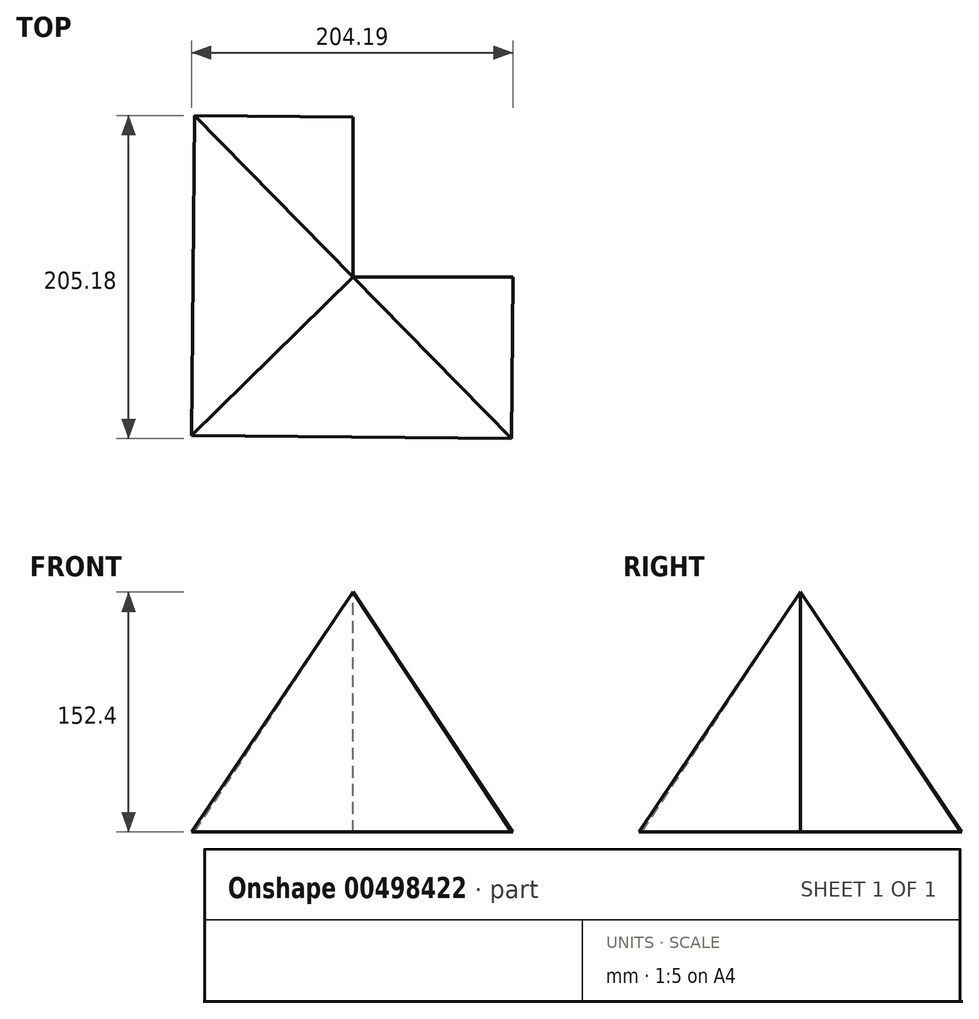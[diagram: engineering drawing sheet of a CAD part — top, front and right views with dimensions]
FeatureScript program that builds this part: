
annotation { "Feature Type Name" : "Feature", "Feature Type Description" : "" }
export const myFeature = defineFeature(function(context is Context, id is Id, definition is map)
    precondition{}
    {
        {
            var Q0;
            Q0=qCreatedBy(makeId("Top.planeOp"),FACE);
            var sketch = newSketch(context, id + "F0", { "sketchPlane" : qUnion([Q0])});
            skCircle(sketch, "E0.cCircle", {"center": v(0, 0) * mm, "radius": 143.68 * mm, "construction": true});
            skLineSegment(sketch, "E0.0", {"start": v(-100.6, 102.6) * mm, "end": v(102.6, 100.6) * mm});
            skLineSegment(sketch, "E0.1", {"start": v(102.6, 100.6) * mm, "end": v(100.6, -102.6) * mm});
            skLineSegment(sketch, "E0.2", {"start": v(100.6, -102.6) * mm, "end": v(-102.6, -100.6) * mm});
            skLineSegment(sketch, "E0.3", {"start": v(-102.6, -100.6) * mm, "end": v(-100.6, 102.6) * mm});
            skSolve(sketch);
        }
        {
            var Q0;
            Q0=qCreatedBy(makeId("Top.planeOp"),FACE);
            cPlane(context, id + "F1", {"entities" : qUnion([Q0]), "cplaneType" : CPlaneType.OFFSET, "offset" : 152.4 * mm, "width" : 152.4 * mm, "height" : 152.4 * mm});
        }
        {
            var Q0;
            Q0=qCreatedBy(id+"F1.planeOp",FACE);
            var sketch = newSketch(context, id + "F2", { "sketchPlane" : qUnion([Q0])});
            skPoint(sketch, "E1", {"position": v(0, 0) * mm});
            skSolve(sketch);
        }
        {
            var Q0;
            Q0=makeQuery(id+"F0.imprint","IMPRINT",FACE,{"disambiguationData":[TD([[makeQuery(id+"F0.imprint","IMPRINT",EDGE,{"derivedFrom":sQuery(id+"F0.wireOp",EDGE,"E0.0")}),-1.0]])]});
            var Q1;
            Q1=sQuery(id+"F2.wireOp",VERTEX,"E1");
            loft(context, id + "F3", {"sheetProfilesArray" : [{ "sheetProfileEntities" : qUnion([Q0]) }, { "sheetProfileEntities" : qUnion([Q1]) }]});
        }
        {
            var Q0;
            Q0=qCreatedBy(id+"F1.planeOp",FACE);
            var sketch = newSketch(context, id + "F4", { "sketchPlane" : qUnion([Q0])});
            skLineSegment(sketch, "E2.bottom", {"start": v(0, 0) * mm, "end": v(118.51, 0) * mm});
            skLineSegment(sketch, "E2.top", {"start": v(0, 111.65) * mm, "end": v(118.51, 111.65) * mm});
            skLineSegment(sketch, "E2.left", {"start": v(0, 0) * mm, "end": v(0, 111.65) * mm});
            skLineSegment(sketch, "E2.right", {"start": v(118.51, 0) * mm, "end": v(118.51, 111.65) * mm});
            skLineSegment(sketch, "E3.bottom", {"start": v(114.2, 111.65) * mm, "end": v(118.51, 111.65) * mm});
            skLineSegment(sketch, "E3.top", {"start": v(114.2, 107.33) * mm, "end": v(118.51, 107.33) * mm});
            skLineSegment(sketch, "E3.left", {"start": v(118.51, 107.33) * mm, "end": v(118.51, 111.65) * mm});
            skLineSegment(sketch, "E3.right", {"start": v(114.2, 107.33) * mm, "end": v(114.2, 111.65) * mm});
            skSolve(sketch);
        }
        {
            var Q0;
            Q0=makeQuery(id+"F4.imprint","IMPRINT",FACE,{"disambiguationData":[TD([[makeQuery(id+"F4.imprint","IMPRINT",EDGE,{"derivedFrom":sQuery(id+"F4.wireOp",EDGE,"E2.bottom")}),1.0]])]});
            var Q1;
            Q1=makeQuery(id+"F4.imprint","IMPRINT",FACE,{"disambiguationData":[TD([[makeQuery(id+"F4.imprint","IMPRINT",EDGE,{"derivedFrom":sQuery(id+"F4.wireOp",EDGE,"E3.bottom")}),-1.0]])]});
            extrude(context, id + "F5", {"entities" : qUnion([Q0, Q1]), "operationType" : NewBodyOperationType.REMOVE, "oppositeDirection" : true, "depth" : 203.2 * mm, "offsetDistance" : 25.4 * mm});
        }
    });
